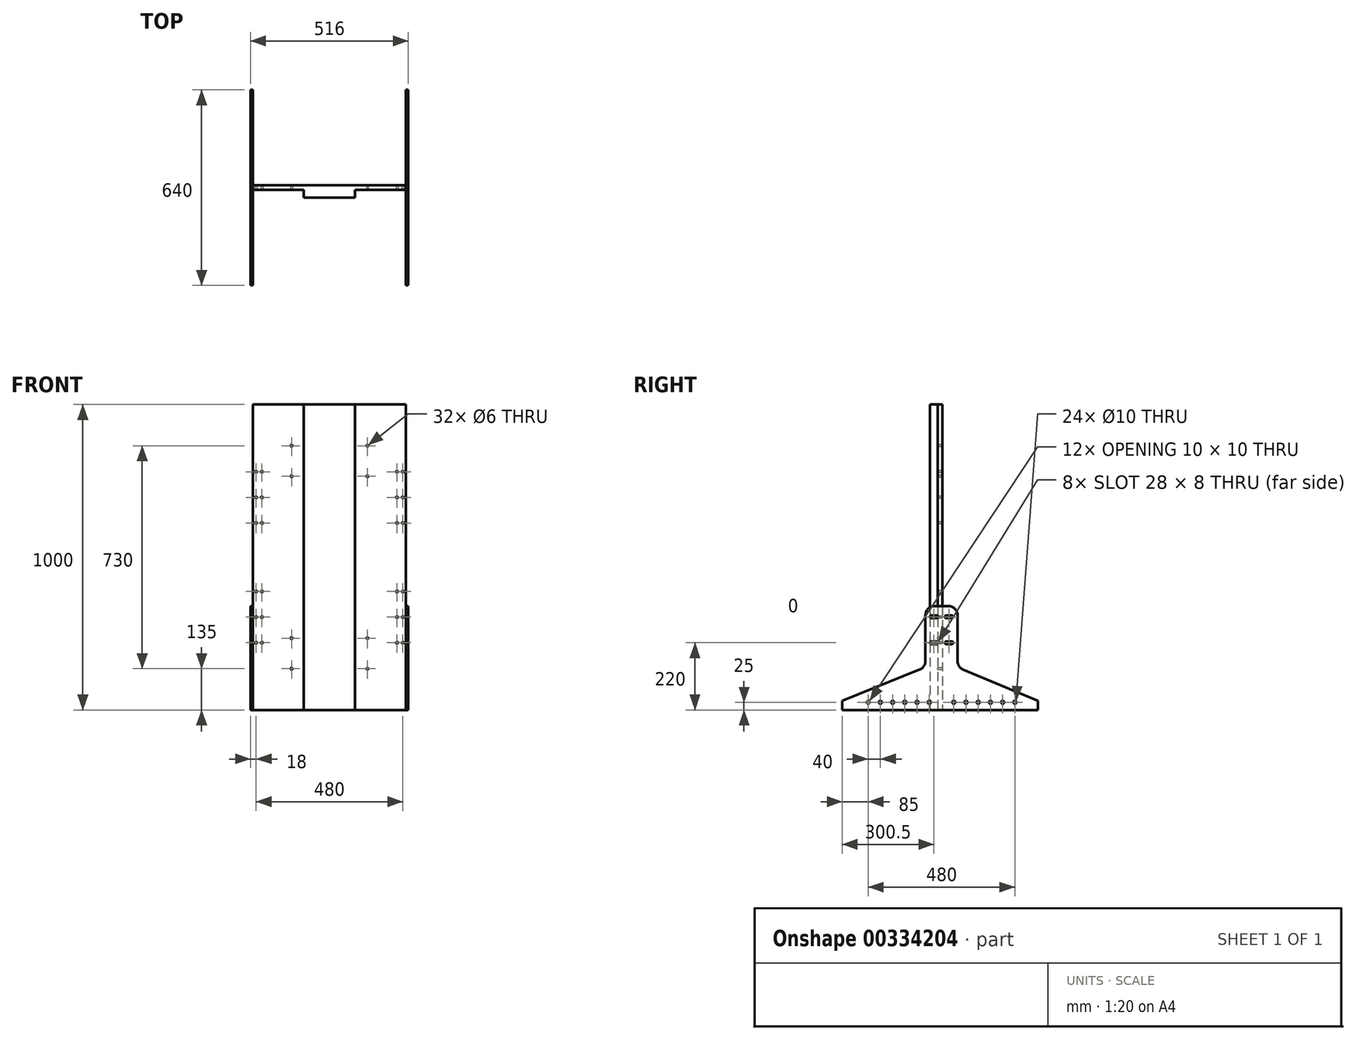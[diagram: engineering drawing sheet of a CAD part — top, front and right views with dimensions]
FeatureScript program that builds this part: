
annotation { "Feature Type Name" : "Feature", "Feature Type Description" : "" }
export const myFeature = defineFeature(function(context is Context, id is Id, definition is map)
    precondition{}
    {
        {
            var Q0;
            Q0=qCreatedBy(makeId("Front.planeOp"),FACE);
            var sketch = newSketch(context, id + "F0", { "sketchPlane" : qUnion([Q0])});
            skLineSegment(sketch, "E0.bottom", {"start": v(250, 500) * mm, "end": v(-250, 500) * mm});
            skLineSegment(sketch, "E0.top", {"start": v(250, -500) * mm, "end": v(-250, -500) * mm});
            skLineSegment(sketch, "E0.left", {"start": v(250, 500) * mm, "end": v(250, -500) * mm});
            skLineSegment(sketch, "E0.right", {"start": v(-250, 500) * mm, "end": v(-250, -500) * mm});
            skPoint(sketch, "E0.middle", {"position": v(0, 0) * mm});
            skSolve(sketch);
        }
        {
            var Q0;
            Q0 = qSketchRegion(id + "F0", true);
            extrude(context, id + "F1", {"entities" : qUnion([Q0]), "depth" : 15 * mm});
        }
        {
            var Q0;
            Q0=makeQuery(id+"F1.opExtrude","CAP_FACE",FACE,{"disambiguationData":[OSD([sQuery(id+"F0.wireOp",EDGE,"E0.bottom"),sQuery(id+"F0.wireOp",EDGE,"E0.top"),sQuery(id+"F0.wireOp",EDGE,"E0.left"),sQuery(id+"F0.wireOp",EDGE,"E0.right")])],"isStart":false});
            var sketch = newSketch(context, id + "F2", { "sketchPlane" : qUnion([Q0])});
            skLineSegment(sketch, "E1.bottom", {"start": v(84, 500) * mm, "end": v(-84, 500) * mm});
            skLineSegment(sketch, "E1.top", {"start": v(84, -500) * mm, "end": v(-84, -500) * mm});
            skLineSegment(sketch, "E1.left", {"start": v(84, 500) * mm, "end": v(84, -500) * mm});
            skLineSegment(sketch, "E1.right", {"start": v(-84, 500) * mm, "end": v(-84, -500) * mm});
            skPoint(sketch, "E1.middle", {"position": v(0, 0) * mm});
            skSolve(sketch);
        }
        {
            var Q0;
            Q0 = qSketchRegion(id + "F2", true);
            extrude(context, id + "F3", {"entities" : qUnion([Q0]), "operationType" : NewBodyOperationType.ADD, "depth" : 25 * mm});
        }
        {
            var Q0;
            {var subQ0=sQuery(id+"F0.wireOp",EDGE,"E0.top");var subQ1=sQuery(id+"F0.wireOp",EDGE,"E0.right");var subQ2=sQuery(id+"F0.wireOp",EDGE,"E0.bottom");Q0=makeQuery(id+"F3.boolean.opBoolean","SPLIT",FACE,{"disambiguationData":[TD([makeQuery(id+"F1.opExtrude","SWEPT_FACE",FACE,{"disambiguationData":[OSD([subQ1])]})])],"derivedFrom":makeQuery(id+"F1.opExtrude","CAP_FACE",FACE,{"disambiguationData":[OSD([subQ2,subQ0,sQuery(id+"F0.wireOp",EDGE,"E0.left"),subQ1])],"isStart":false})});}
            var sketch = newSketch(context, id + "F4", { "sketchPlane" : qUnion([Q0])});
            skCircle(sketch, "E2", {"center": v(124, -365) * mm, "radius": 3 * mm});
            skCircle(sketch, "E3", {"center": v(124, -265) * mm, "radius": 3 * mm});
            skCircle(sketch, "E4", {"center": v(240, -112) * mm, "radius": 3 * mm});
            skCircle(sketch, "E5.0.1.0", {"center": v(240, -196) * mm, "radius": 3 * mm});
            skCircle(sketch, "E5.0.2.0", {"center": v(240, -280) * mm, "radius": 3 * mm});
            skCircle(sketch, "E5.1.0.0", {"center": v(221, -112) * mm, "radius": 3 * mm});
            skCircle(sketch, "E5.1.1.0", {"center": v(221, -196) * mm, "radius": 3 * mm});
            skCircle(sketch, "E5.1.2.0", {"center": v(221, -280) * mm, "radius": 3 * mm});
            skLineSegment(sketch, "E5.direction1", {"start": v(240, -112) * mm, "end": v(221, -112) * mm, "construction": true});
            skLineSegment(sketch, "E5.direction2", {"start": v(240, -112) * mm, "end": v(240, -196) * mm, "construction": true});
            skLineSegment(sketch, "E6.MirrorCS", {"start": v(-240, -112) * mm, "end": v(-221, -112) * mm, "construction": true});
            skCircle(sketch, "E7.MirrorC", {"center": v(-221, -112) * mm, "radius": 3 * mm});
            skCircle(sketch, "E8.MirrorC", {"center": v(-240, -112) * mm, "radius": 3 * mm});
            skCircle(sketch, "E9.MirrorC", {"center": v(-124, -265) * mm, "radius": 3 * mm});
            skCircle(sketch, "E10.MirrorC", {"center": v(-240, -196) * mm, "radius": 3 * mm});
            skCircle(sketch, "E11.MirrorC", {"center": v(-124, -365) * mm, "radius": 3 * mm});
            skLineSegment(sketch, "E12.MirrorCS", {"start": v(-240, -112) * mm, "end": v(-240, -196) * mm, "construction": true});
            skCircle(sketch, "E13.MirrorC", {"center": v(-221, -280) * mm, "radius": 3 * mm});
            skCircle(sketch, "E14.MirrorC", {"center": v(-221, -196) * mm, "radius": 3 * mm});
            skCircle(sketch, "E15.MirrorC", {"center": v(-240, -280) * mm, "radius": 3 * mm});
            skLineSegment(sketch, "E16.MirrorCS", {"start": v(240, 112) * mm, "end": v(221, 112) * mm, "construction": true});
            skCircle(sketch, "E17.MirrorC", {"center": v(240, 112) * mm, "radius": 3 * mm});
            skCircle(sketch, "E18.MirrorC", {"center": v(221, 112) * mm, "radius": 3 * mm});
            skLineSegment(sketch, "E19.MirrorCS", {"start": v(-240, 112) * mm, "end": v(-221, 112) * mm, "construction": true});
            skCircle(sketch, "E20.MirrorC", {"center": v(-240, 112) * mm, "radius": 3 * mm});
            skCircle(sketch, "E21.MirrorC", {"center": v(-221, 112) * mm, "radius": 3 * mm});
            skCircle(sketch, "E22.MirrorC", {"center": v(-221, 196) * mm, "radius": 3 * mm});
            skCircle(sketch, "E23.MirrorC", {"center": v(221, 196) * mm, "radius": 3 * mm});
            skCircle(sketch, "E24.MirrorC", {"center": v(-240, 196) * mm, "radius": 3 * mm});
            skCircle(sketch, "E25.MirrorC", {"center": v(124, 265) * mm, "radius": 3 * mm});
            skCircle(sketch, "E26.MirrorC", {"center": v(240, 196) * mm, "radius": 3 * mm});
            skCircle(sketch, "E27.MirrorC", {"center": v(221, 280) * mm, "radius": 3 * mm});
            skLineSegment(sketch, "E28.MirrorCS", {"start": v(240, 112) * mm, "end": v(240, 196) * mm, "construction": true});
            skCircle(sketch, "E29.MirrorC", {"center": v(-124, 265) * mm, "radius": 3 * mm});
            skCircle(sketch, "E30.MirrorC", {"center": v(-124, 365) * mm, "radius": 3 * mm});
            skCircle(sketch, "E31.MirrorC", {"center": v(-240, 280) * mm, "radius": 3 * mm});
            skCircle(sketch, "E32.MirrorC", {"center": v(-221, 280) * mm, "radius": 3 * mm});
            skCircle(sketch, "E33.MirrorC", {"center": v(124, 365) * mm, "radius": 3 * mm});
            skCircle(sketch, "E34.MirrorC", {"center": v(240, 280) * mm, "radius": 3 * mm});
            skLineSegment(sketch, "E35.MirrorCS", {"start": v(-240, 112) * mm, "end": v(-240, 196) * mm, "construction": true});
            skSolve(sketch);
        }
        {
            var Q0;
            Q0 = qSketchRegion(id + "F4", true);
            extrude(context, id + "F5", {"entities" : qUnion([Q0]), "operationType" : NewBodyOperationType.REMOVE, "oppositeDirection" : true, "depth" : 25 * mm});
        }
        {
            var Q0;
            Q0=makeQuery(id+"F1.opExtrude","SWEPT_FACE",FACE,{"disambiguationData":[OSD([sQuery(id+"F0.wireOp",EDGE,"E0.right")])]});
            var sketch = newSketch(context, id + "F6", { "sketchPlane" : qUnion([Q0])});
            skLineSegment(sketch, "E36", {"start": v(264.54, -500) * mm, "end": v(327.5, -500) * mm});
            skPoint(sketch, "E36.endSnap0", {"position": v(7.5, -500) * mm});
            skLineSegment(sketch, "E37", {"start": v(327.5, -500) * mm, "end": v(327.5, -470) * mm});
            skLineSegment(sketch, "E38", {"start": v(327.5, -470) * mm, "end": v(73.77, -367.58) * mm});
            skLineSegment(sketch, "E39", {"start": v(55, -339.76) * mm, "end": v(55, -190) * mm});
            skLineSegment(sketch, "E40", {"start": v(25, -160) * mm, "end": v(15, -160) * mm});
            skLineSegment(sketch, "E41", {"start": v(-165.6, -500) * mm, "end": v(-312.5, -500) * mm});
            skLineSegment(sketch, "E42", {"start": v(-312.5, -500) * mm, "end": v(-312.5, -470) * mm});
            skLineSegment(sketch, "E43", {"start": v(-312.5, -470) * mm, "end": v(-68.4, -367.71) * mm});
            skLineSegment(sketch, "E44", {"start": v(-50, -340.04) * mm, "end": v(-50, -190) * mm});
            skLineSegment(sketch, "E45", {"start": v(-20, -160) * mm, "end": v(15, -160) * mm});
            skPoint(sketch, "E46.visualSharp", {"position": v(-50, -160) * mm});
            skArc(sketch, "E46.filletArc", {"start": v(-20, -160) * mm, "mid": v(-41.21, -168.79) * mm, "end": v(-50, -190) * mm});
            skPoint(sketch, "E47.visualSharp", {"position": v(55, -160) * mm});
            skArc(sketch, "E47.filletArc", {"start": v(55, -190) * mm, "mid": v(46.21, -168.79) * mm, "end": v(25, -160) * mm});
            skPoint(sketch, "E48.visualSharp", {"position": v(-50, -360) * mm});
            skArc(sketch, "E48.filletArc", {"start": v(-68.4, -367.71) * mm, "mid": v(-55.02, -356.66) * mm, "end": v(-50, -340.04) * mm});
            skPoint(sketch, "E49.visualSharp", {"position": v(55, -360) * mm});
            skArc(sketch, "E49.filletArc", {"start": v(55, -339.76) * mm, "mid": v(60.13, -356.54) * mm, "end": v(73.77, -367.58) * mm});
            skPoint(sketch, "E50.visualSharp", {"position": v(7.5, -410) * mm});
            skPoint(sketch, "E51.newPointA", {"position": v(247.5, -497) * mm});
            skLineSegment(sketch, "E52", {"start": v(-165.6, -500) * mm, "end": v(264.54, -500) * mm});
            skSolve(sketch);
        }
        {
            var Q0;
            Q0 = qSketchRegion(id + "F6", true);
            extrude(context, id + "F7", {"entities" : qUnion([Q0]), "depth" : 8 * mm});
        }
        {
            var Q0;
            Q0=makeQuery(id+"F7.opExtrude","CAP_FACE",FACE,{"disambiguationData":[OSD([sQuery(id+"F6.wireOp",EDGE,"E36"),sQuery(id+"F6.wireOp",EDGE,"E37"),sQuery(id+"F6.wireOp",EDGE,"E38"),sQuery(id+"F6.wireOp",EDGE,"E39"),sQuery(id+"F6.wireOp",EDGE,"E40"),sQuery(id+"F6.wireOp",EDGE,"E41"),sQuery(id+"F6.wireOp",EDGE,"E42"),sQuery(id+"F6.wireOp",EDGE,"E43"),sQuery(id+"F6.wireOp",EDGE,"E44"),sQuery(id+"F6.wireOp",EDGE,"E45"),sQuery(id+"F6.wireOp",EDGE,"E46.filletArc"),sQuery(id+"F6.wireOp",EDGE,"E47.filletArc"),sQuery(id+"F6.wireOp",EDGE,"E48.filletArc"),sQuery(id+"F6.wireOp",EDGE,"E49.filletArc")])],"isStart":true});
            var sketch = newSketch(context, id + "F8", { "sketchPlane" : qUnion([Q0])});
            skPoint(sketch, "E53", {"position": v(12, -280) * mm});
            skArc(sketch, "E54", {"start": v(12, -276) * mm, "mid": v(8, -280) * mm, "end": v(12, -284) * mm});
            skLineSegment(sketch, "E55", {"start": v(12, -276) * mm, "end": v(32, -276) * mm});
            skArc(sketch, "E56", {"start": v(32, -276) * mm, "mid": v(36, -280) * mm, "end": v(32, -284) * mm});
            skLineSegment(sketch, "E57", {"start": v(12, -284) * mm, "end": v(32, -284) * mm});
            skLineSegment(sketch, "E58.0.1.0", {"start": v(12, -191) * mm, "end": v(32, -191) * mm});
            skLineSegment(sketch, "E58.0.1.1", {"start": v(12, -199) * mm, "end": v(32, -199) * mm});
            skArc(sketch, "E58.0.1.2", {"start": v(32, -191) * mm, "mid": v(36, -195) * mm, "end": v(32, -199) * mm});
            skArc(sketch, "E58.0.1.3", {"start": v(12, -191) * mm, "mid": v(8, -195) * mm, "end": v(12, -199) * mm});
            skPoint(sketch, "E58.0.1.4", {"position": v(12, -195) * mm});
            skLineSegment(sketch, "E58.direction1", {"start": v(12, -284) * mm, "end": v(55, -284) * mm, "construction": true});
            skLineSegment(sketch, "E58.direction2", {"start": v(12, -284) * mm, "end": v(12, -199) * mm, "construction": true});
            skLineSegment(sketch, "E59", {"start": v(-2.5, -160) * mm, "end": v(-2.5, -500) * mm});
            skArc(sketch, "E60.MirrorCS", {"start": v(-37, -276) * mm, "mid": v(-41, -280) * mm, "end": v(-37, -284) * mm});
            skArc(sketch, "E61.MirrorCS", {"start": v(-17, -191) * mm, "mid": v(-13, -195) * mm, "end": v(-17, -199) * mm});
            skArc(sketch, "E62.MirrorCS", {"start": v(-37, -191) * mm, "mid": v(-41, -195) * mm, "end": v(-37, -199) * mm});
            skArc(sketch, "E63.MirrorCS", {"start": v(-17, -276) * mm, "mid": v(-13, -280) * mm, "end": v(-17, -284) * mm});
            skLineSegment(sketch, "E64.MirrorCS", {"start": v(-17, -284) * mm, "end": v(-37, -284) * mm});
            skLineSegment(sketch, "E65.MirrorCS", {"start": v(-17, -284) * mm, "end": v(-17, -199) * mm, "construction": true});
            skLineSegment(sketch, "E66.MirrorCS", {"start": v(-17, -284) * mm, "end": v(-60, -284) * mm, "construction": true});
            skLineSegment(sketch, "E67.MirrorCS", {"start": v(-17, -276) * mm, "end": v(-37, -276) * mm});
            skLineSegment(sketch, "E68.MirrorCS", {"start": v(-17, -191) * mm, "end": v(-37, -191) * mm});
            skLineSegment(sketch, "E69.MirrorCS", {"start": v(-17, -199) * mm, "end": v(-37, -199) * mm});
            skCircle(sketch, "E70", {"center": v(-42.5, -475) * mm, "radius": 5 * mm});
            skCircle(sketch, "E71.1.0.0", {"center": v(-82.5, -475) * mm, "radius": 5 * mm});
            skCircle(sketch, "E71.2.0.0", {"center": v(-122.5, -475) * mm, "radius": 5 * mm});
            skCircle(sketch, "E71.3.0.0", {"center": v(-162.5, -475) * mm, "radius": 5 * mm});
            skCircle(sketch, "E71.4.0.0", {"center": v(-202.5, -475) * mm, "radius": 5 * mm});
            skCircle(sketch, "E71.5.0.0", {"center": v(-242.5, -475) * mm, "radius": 5 * mm});
            skLineSegment(sketch, "E71.direction1", {"start": v(-42.5, -475) * mm, "end": v(-82.5, -475) * mm, "construction": true});
            skCircle(sketch, "E72.MirrorC", {"center": v(37.5, -475) * mm, "radius": 5 * mm});
            skCircle(sketch, "E73.MirrorC", {"center": v(157.5, -475) * mm, "radius": 5 * mm});
            skCircle(sketch, "E74.MirrorC", {"center": v(237.5, -475) * mm, "radius": 5 * mm});
            skCircle(sketch, "E75.MirrorC", {"center": v(77.5, -475) * mm, "radius": 5 * mm});
            skCircle(sketch, "E76.MirrorC", {"center": v(197.5, -475) * mm, "radius": 5 * mm});
            skLineSegment(sketch, "E77.MirrorCS", {"start": v(37.5, -475) * mm, "end": v(77.5, -475) * mm, "construction": true});
            skCircle(sketch, "E78.MirrorC", {"center": v(117.5, -475) * mm, "radius": 5 * mm});
            skSolve(sketch);
        }
        {
            var Q0;
            Q0 = qSketchRegion(id + "F8", true);
            extrude(context, id + "F9", {"entities" : qUnion([Q0]), "operationType" : NewBodyOperationType.REMOVE, "oppositeDirection" : true, "depth" : 25 * mm});
        }
        {
            var Q0;
            Q0=makeQuery(id+"F7.opExtrude","SWEPT_BODY",BODY,{"disambiguationData":[OSD([sQuery(id+"F6.wireOp",EDGE,"E36"),sQuery(id+"F6.wireOp",EDGE,"E37"),sQuery(id+"F6.wireOp",EDGE,"E38"),sQuery(id+"F6.wireOp",EDGE,"E39"),sQuery(id+"F6.wireOp",EDGE,"E40"),sQuery(id+"F6.wireOp",EDGE,"E41"),sQuery(id+"F6.wireOp",EDGE,"E42"),sQuery(id+"F6.wireOp",EDGE,"E43"),sQuery(id+"F6.wireOp",EDGE,"E44"),sQuery(id+"F6.wireOp",EDGE,"E45"),sQuery(id+"F6.wireOp",EDGE,"E46.filletArc"),sQuery(id+"F6.wireOp",EDGE,"E47.filletArc"),sQuery(id+"F6.wireOp",EDGE,"E48.filletArc"),sQuery(id+"F6.wireOp",EDGE,"E49.filletArc")])]});
            var Q1;
            Q1=qCreatedBy(makeId("Right.planeOp"),FACE);
            mirror(context, id + "F10", {"entities" : qUnion([Q0]), "mirrorPlane" : qUnion([Q1])});
        }
    });
